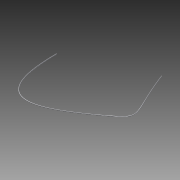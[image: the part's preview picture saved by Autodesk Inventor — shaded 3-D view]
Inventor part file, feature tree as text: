
AUTODESK INVENTOR PART (.ipt)
format: ipt  version: 2012 SP2 (Build 160219200, 219)  size: 114,688 bytes
history: native  units: in
note: dims shown in document units (in); Inventor stores cm internally (conversion verified against a paired STEP export)
features: sketch x2, sweep x1
ambient origin geometry x8: Origin, YZ Plane, XZ Plane, XY Plane, X Axis, Y Axis, Z Axis, Center Point
bodies: Solid1 (feature_tree)
feature tree (3):
  sweep  "Sweep1"
  sketch  "Sketch1"  dims[d1=0.0in]
  sketch  "3D Sketch1"
